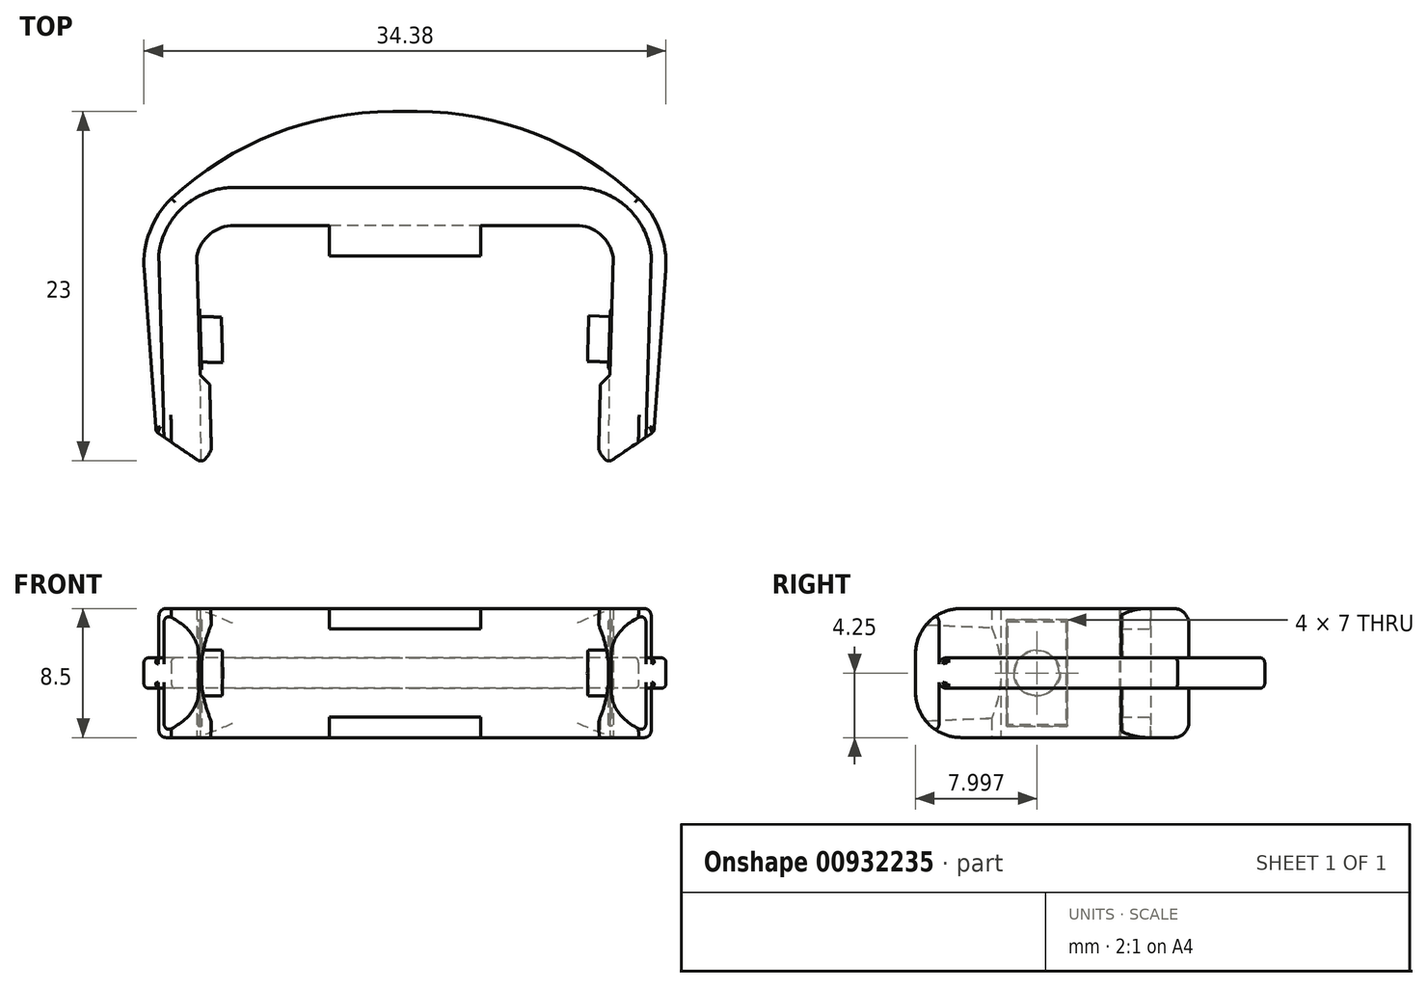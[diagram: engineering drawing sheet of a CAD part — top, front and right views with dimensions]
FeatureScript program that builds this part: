
annotation { "Feature Type Name" : "Feature", "Feature Type Description" : "" }
export const myFeature = defineFeature(function(context is Context, id is Id, definition is map)
    precondition{}
    {
        {
            var Q0;
            Q0=qCreatedBy(makeId("Top.planeOp"),FACE);
            var sketch = newSketch(context, id + "F0", { "sketchPlane" : qUnion([Q0])});
            skLineSegment(sketch, "E0", {"start": v(13.34, 0) * mm, "end": v(13.72, 13.41) * mm});
            skLineSegment(sketch, "E1", {"start": v(-13.34, 0) * mm, "end": v(-13.7, 13.5) * mm});
            skLineSegment(sketch, "E2", {"start": v(-11.25, 15.5) * mm, "end": v(11.25, 15.5) * mm});
            skArc(sketch, "E3", {"start": v(11.25, 15.5) * mm, "mid": v(12.87, 14.9) * mm, "end": v(13.72, 13.41) * mm});
            skArc(sketch, "E4", {"start": v(-11.25, 15.5) * mm, "mid": v(-12.83, 14.93) * mm, "end": v(-13.7, 13.5) * mm});
            skLineSegment(sketch, "E5", {"start": v(15.84, 0) * mm, "end": v(16.22, 13.55) * mm});
            skLineSegment(sketch, "E6", {"start": v(-11.25, 18) * mm, "end": v(11.25, 18) * mm});
            skLineSegment(sketch, "E7", {"start": v(-15.84, 0) * mm, "end": v(-16.2, 13.66) * mm});
            skLineSegment(sketch, "E8", {"start": v(-15.84, 0) * mm, "end": v(-13.33, 0) * mm});
            skLineSegment(sketch, "E9", {"start": v(13.34, 0) * mm, "end": v(15.84, 0) * mm});
            skLineSegment(sketch, "E10", {"start": v(-13.6, 0) * mm, "end": v(-18, 3) * mm});
            skLineSegment(sketch, "E11", {"start": v(13.6, 0) * mm, "end": v(18, 3) * mm});
            skLineSegment(sketch, "E12", {"start": v(-12.73, 0) * mm, "end": v(-12.87, 5) * mm});
            skLineSegment(sketch, "E13", {"start": v(12.74, 0) * mm, "end": v(12.88, 5) * mm});
            skLineSegment(sketch, "E14", {"start": v(-12.87, 5) * mm, "end": v(-13.49, 5.63) * mm});
            skLineSegment(sketch, "E15", {"start": v(12.88, 5) * mm, "end": v(13.5, 5.63) * mm});
            skLineSegment(sketch, "E16", {"start": v(-12.73, 0) * mm, "end": v(-13.33, 0) * mm});
            skLineSegment(sketch, "E17", {"start": v(12.74, 0) * mm, "end": v(13.34, 0) * mm});
            skArc(sketch, "E18", {"start": v(-11.25, 18) * mm, "mid": v(-14.54, 16.76) * mm, "end": v(-16.2, 13.66) * mm});
            skArc(sketch, "E19", {"start": v(11.25, 18) * mm, "mid": v(14.59, 16.72) * mm, "end": v(16.22, 13.55) * mm});
            skPoint(sketch, "E20", {"position": v(-14.59, 0) * mm});
            skSolve(sketch);
        }
        {
            var Q0;
            Q0 = qSketchRegion(id + "F0", true);
            extrude(context, id + "F1", {"entities" : qUnion([Q0]), "depth" : 8.5 * mm, "offsetDistance" : 25 * mm, "symmetric" : true});
        }
        {
            var Q0;
            Q0=makeQuery(id+"F1.opExtrude","CAP_EDGE",EDGE,{"disambiguationData":[OSD([sQuery(id+"F0.wireOp",EDGE,"E8")])],"isStart":false});
            var Q1;
            Q1=makeQuery(id+"F1.opExtrude","CAP_EDGE",EDGE,{"disambiguationData":[OSD([sQuery(id+"F0.wireOp",EDGE,"E8")])],"isStart":true});
            var Q2;
            Q2=makeQuery(id+"F1.opExtrude","CAP_EDGE",EDGE,{"disambiguationData":[OSD([sQuery(id+"F0.wireOp",EDGE,"E9")])],"isStart":false});
            var Q3;
            Q3=makeQuery(id+"F1.opExtrude","CAP_EDGE",EDGE,{"disambiguationData":[OSD([sQuery(id+"F0.wireOp",EDGE,"E9")])],"isStart":true});
            fillet(context, id + "F2", {"entities" : qUnion([Q0, Q1, Q2, Q3]), "radius" : 3 * mm, "tangentPropagation" : true, "allowEdgeOverflow" : false});
        }
        {
            var Q0;
            Q0=makeQuery(id+"F1.opExtrude","CAP_EDGE",EDGE,{"disambiguationData":[OSD([sQuery(id+"F0.wireOp",EDGE,"E6")])],"isStart":false});
            var Q1;
            Q1=makeQuery(id+"F1.opExtrude","CAP_EDGE",EDGE,{"disambiguationData":[OSD([sQuery(id+"F0.wireOp",EDGE,"E6")])],"isStart":true});
            fillet(context, id + "F3", {"entities" : qUnion([Q0, Q1]), "radius" : 1 * mm, "allowEdgeOverflow" : false});
        }
        {
            var Q0;
            Q0=makeQuery(id+"F1.opExtrude","CAP_EDGE",EDGE,{"disambiguationData":[OSD([sQuery(id+"F0.wireOp",EDGE,"E7")])],"isStart":true});
            var Q1;
            Q1=makeQuery(id+"F1.opExtrude","CAP_EDGE",EDGE,{"disambiguationData":[OSD([sQuery(id+"F0.wireOp",EDGE,"e52e7ded-89c3-43d7-ae40-fe6d7447af5a")])],"isStart":true});
            var Q2;
            Q2=makeQuery(id+"F1.opExtrude","CAP_EDGE",EDGE,{"disambiguationData":[OSD([sQuery(id+"F0.wireOp",EDGE,"E5")])],"isStart":true});
            var Q3;
            Q3=makeQuery(id+"F1.opExtrude","CAP_EDGE",EDGE,{"disambiguationData":[OSD([sQuery(id+"F0.wireOp",EDGE,"fc301240-3a13-4fbf-9681-00e86052290d")])],"isStart":true});
            var Q4;
            Q4=makeQuery(id+"F1.opExtrude","CAP_EDGE",EDGE,{"disambiguationData":[OSD([sQuery(id+"F0.wireOp",EDGE,"e52e7ded-89c3-43d7-ae40-fe6d7447af5a")])],"isStart":false});
            var Q5;
            Q5=makeQuery(id+"F1.opExtrude","CAP_EDGE",EDGE,{"disambiguationData":[OSD([sQuery(id+"F0.wireOp",EDGE,"E7")])],"isStart":false});
            var Q6;
            Q6=makeQuery(id+"F1.opExtrude","CAP_EDGE",EDGE,{"disambiguationData":[OSD([sQuery(id+"F0.wireOp",EDGE,"fc301240-3a13-4fbf-9681-00e86052290d")])],"isStart":false});
            var Q7;
            Q7=makeQuery(id+"F1.opExtrude","CAP_EDGE",EDGE,{"disambiguationData":[OSD([sQuery(id+"F0.wireOp",EDGE,"E5")])],"isStart":false});
            fillet(context, id + "F4", {"entities" : qUnion([Q0, Q1, Q2, Q3, Q4, Q5, Q6, Q7]), "radius" : .5 * mm, "tangentPropagation" : true, "allowEdgeOverflow" : false});
        }
        {
            var Q0;
            {var subQ0=sQuery(id+"F0.wireOp",EDGE,"E8");var subQ1=sQuery(id+"F0.wireOp",EDGE,"E7");var subQ2=makeQuery(id+"F0.imprint","INTERSECT",VERTEX,{"derivedFrom":[subQ1,subQ0]});Q0=makeQuery(id+"F0.imprint","IMPRINT",FACE,{"disambiguationData":[TD([[makeQuery(id+"F0.imprint","IMPRINT",EDGE,{"disambiguationData":[TD([[subQ2,-1.0]])],"derivedFrom":subQ1}),-1.0]])]});}
            var Q1;
            {var subQ0=sQuery(id+"F0.wireOp",EDGE,"E9");var subQ1=sQuery(id+"F0.wireOp",EDGE,"E5");var subQ2=makeQuery(id+"F0.imprint","INTERSECT",VERTEX,{"derivedFrom":[subQ1,subQ0]});Q1=makeQuery(id+"F0.imprint","IMPRINT",FACE,{"disambiguationData":[TD([[makeQuery(id+"F0.imprint","IMPRINT",EDGE,{"disambiguationData":[TD([[subQ2,-1.0]])],"derivedFrom":subQ1}),1.0]])]});}
            extrude(context, id + "F5", {"entities" : qUnion([Q0, Q1]), "operationType" : NewBodyOperationType.REMOVE, "oppositeDirection" : true, "depth" : 25 * mm, "offsetDistance" : 25 * mm, "symmetric" : true});
        }
        {
            var Q0;
            Q0=qCreatedBy(makeId("Front.planeOp"),FACE);
            var sketch = newSketch(context, id + "F6", { "sketchPlane" : qUnion([Q0])});
            skCircle(sketch, "E21", {"center": v(-5.68, 0) * mm, "radius": 7.75 * mm});
            skCircle(sketch, "E22", {"center": v(5.68, 0) * mm, "radius": 7.75 * mm});
            skSolve(sketch);
        }
        {
            var Q0;
            Q0 = qSketchRegion(id + "F6", true);
            extrude(context, id + "F7", {"entities" : qUnion([Q0]), "operationType" : NewBodyOperationType.REMOVE, "oppositeDirection" : true, "depth" : 5.7 * mm, "offsetDistance" : 25 * mm, "hasDraft" : true, "draftAngle" : .5 * degree});
        }
        {
            var Q0;
            Q0=makeQuery(id+"F1.opExtrude","SWEPT_FACE",FACE,{"disambiguationData":[OSD([sQuery(id+"F0.wireOp",EDGE,"E1")])]});
            var sketch = newSketch(context, id + "F8", { "sketchPlane" : qUnion([Q0])});
            skLineSegment(sketch, "E23.bottom", {"start": v(6.36, 3.5) * mm, "end": v(10.36, 3.5) * mm});
            skLineSegment(sketch, "E23.top", {"start": v(6.36, -3.5) * mm, "end": v(10.36, -3.5) * mm});
            skLineSegment(sketch, "E23.left", {"start": v(6.36, 3.5) * mm, "end": v(6.36, -3.5) * mm});
            skLineSegment(sketch, "E23.right", {"start": v(10.36, 3.5) * mm, "end": v(10.36, -3.5) * mm});
            skPoint(sketch, "E23.middle", {"position": v(8.36, 0) * mm});
            skPoint(sketch, "E23.middle.positionSnap0", {"position": v(6, 0) * mm});
            skPoint(sketch, "E23.centerSnap0", {"position": v(6, 0) * mm});
            skCircle(sketch, "E24", {"center": v(8.36, 0) * mm, "radius": 1.5 * mm});
            skSolve(sketch);
        }
        {
            var Q0;
            Q0=makeQuery(id+"F1.opExtrude","SWEPT_FACE",FACE,{"disambiguationData":[OSD([sQuery(id+"F0.wireOp",EDGE,"E0")])]});
            var sketch = newSketch(context, id + "F9", { "sketchPlane" : qUnion([Q0])});
            skLineSegment(sketch, "E25.bottom", {"start": v(-6.38, -3.5) * mm, "end": v(-10.38, -3.5) * mm});
            skLineSegment(sketch, "E25.top", {"start": v(-6.38, 3.5) * mm, "end": v(-10.38, 3.5) * mm});
            skLineSegment(sketch, "E25.left", {"start": v(-6.38, -3.5) * mm, "end": v(-6.38, 3.5) * mm});
            skLineSegment(sketch, "E25.right", {"start": v(-10.38, -3.5) * mm, "end": v(-10.38, 3.5) * mm});
            skPoint(sketch, "E25.middle", {"position": v(-8.38, 0) * mm});
            skCircle(sketch, "E26", {"center": v(-8.38, 0) * mm, "radius": 1.5 * mm});
            skSolve(sketch);
        }
        {
            var Q0;
            Q0=makeQuery(id+"F9.imprint","IMPRINT",FACE,{"disambiguationData":[TD([[makeQuery(id+"F9.imprint","IMPRINT",EDGE,{"derivedFrom":sQuery(id+"F9.wireOp",EDGE,"E26")}),1.0]])]});
            var Q1;
            Q1=makeQuery(id+"F8.imprint","IMPRINT",FACE,{"disambiguationData":[TD([[makeQuery(id+"F8.imprint","IMPRINT",EDGE,{"derivedFrom":sQuery(id+"F8.wireOp",EDGE,"E24")}),1.0]])]});
            extrude(context, id + "F10", {"entities" : qUnion([Q0, Q1]), "operationType" : NewBodyOperationType.ADD, "depth" : 3 * mm, "offsetDistance" : 25 * mm, "symmetric" : true});
        }
        {
            var Q0;
            Q0=makeQuery(id+"F9.imprint","IMPRINT",FACE,{"disambiguationData":[TD([[makeQuery(id+"F9.imprint","IMPRINT",EDGE,{"derivedFrom":sQuery(id+"F9.wireOp",EDGE,"E25.bottom")}),-1.0]])]});
            var Q1;
            Q1=makeQuery(id+"F9.imprint","IMPRINT",FACE,{"disambiguationData":[TD([[makeQuery(id+"F9.imprint","IMPRINT",EDGE,{"derivedFrom":sQuery(id+"F9.wireOp",EDGE,"E26")}),1.0]])]});
            var Q2;
            Q2=makeQuery(id+"F8.imprint","IMPRINT",FACE,{"disambiguationData":[TD([[makeQuery(id+"F8.imprint","IMPRINT",EDGE,{"derivedFrom":sQuery(id+"F8.wireOp",EDGE,"E23.bottom")}),-1.0]])]});
            var Q3;
            Q3=makeQuery(id+"F8.imprint","IMPRINT",FACE,{"disambiguationData":[TD([[makeQuery(id+"F8.imprint","IMPRINT",EDGE,{"derivedFrom":sQuery(id+"F8.wireOp",EDGE,"E24")}),1.0]])]});
            extrude(context, id + "F11", {"entities" : qUnion([Q0, Q1, Q2, Q3]), "operationType" : NewBodyOperationType.ADD, "depth" : .2 * mm, "offsetDistance" : 25 * mm, "symmetric" : true});
        }
        {
            var Q0;
            Q0=makeQuery(id+"F11.opExtrude","CAP_EDGE",EDGE,{"disambiguationData":[OSD([sQuery(id+"F9.wireOp",EDGE,"E25.right")])],"isStart":false});
            var Q1;
            Q1=makeQuery(id+"F11.opExtrude","CAP_EDGE",EDGE,{"disambiguationData":[OSD([sQuery(id+"F9.wireOp",EDGE,"E25.bottom")])],"isStart":false});
            var Q2;
            Q2=makeQuery(id+"F11.opExtrude","CAP_EDGE",EDGE,{"disambiguationData":[OSD([sQuery(id+"F9.wireOp",EDGE,"E25.left")])],"isStart":false});
            var Q3;
            Q3=makeQuery(id+"F11.opExtrude","CAP_EDGE",EDGE,{"disambiguationData":[OSD([sQuery(id+"F9.wireOp",EDGE,"E25.top")])],"isStart":false});
            var Q4;
            Q4=makeQuery(id+"F11.opExtrude","CAP_EDGE",EDGE,{"disambiguationData":[OSD([sQuery(id+"F8.wireOp",EDGE,"E23.right")]),OD(1.0)],"isStart":false});
            var Q5;
            Q5=makeQuery(id+"F11.opExtrude","CAP_EDGE",EDGE,{"disambiguationData":[OSD([sQuery(id+"F8.wireOp",EDGE,"E23.bottom")]),OD(1.0)],"isStart":false});
            var Q6;
            Q6=makeQuery(id+"F11.opExtrude","CAP_EDGE",EDGE,{"disambiguationData":[OSD([sQuery(id+"F8.wireOp",EDGE,"E23.top")]),OD(1.0)],"isStart":false});
            var Q7;
            Q7=makeQuery(id+"F11.opExtrude","CAP_EDGE",EDGE,{"disambiguationData":[OSD([sQuery(id+"F8.wireOp",EDGE,"E23.left")]),OD(1.0)],"isStart":false});
            chamfer(context, id + "F12", {"entities" : qUnion([Q0, Q1, Q2, Q3, Q4, Q5, Q6, Q7]), "width" : .1 * mm, "tangentPropagation" : true});
        }
        {
            var Q0;
            Q0=makeQuery(id+"F1.opExtrude","SWEPT_FACE",FACE,{"disambiguationData":[OSD([sQuery(id+"F0.wireOp",EDGE,"E2")])]});
            var sketch = newSketch(context, id + "F13", { "sketchPlane" : qUnion([Q0])});
            skLineSegment(sketch, "E27.bottom", {"start": v(4.98, 2.9) * mm, "end": v(-4.99, 2.9) * mm});
            skLineSegment(sketch, "E27.top", {"start": v(4.98, 4.25) * mm, "end": v(-4.99, 4.25) * mm});
            skLineSegment(sketch, "E27.left", {"start": v(4.98, 2.9) * mm, "end": v(4.98, 4.25) * mm});
            skLineSegment(sketch, "E27.right", {"start": v(-4.99, 2.9) * mm, "end": v(-4.99, 4.25) * mm});
            skPoint(sketch, "E27.middle", {"position": v(0, 3.58) * mm});
            skLineSegment(sketch, "E28.bottom", {"start": v(4.99, -4.25) * mm, "end": v(-4.99, -4.25) * mm});
            skLineSegment(sketch, "E28.top", {"start": v(4.99, -2.9) * mm, "end": v(-4.99, -2.9) * mm});
            skLineSegment(sketch, "E28.left", {"start": v(4.99, -4.25) * mm, "end": v(4.99, -2.9) * mm});
            skLineSegment(sketch, "E28.right", {"start": v(-4.99, -4.25) * mm, "end": v(-4.99, -2.9) * mm});
            skPoint(sketch, "E28.middle", {"position": v(0, -3.58) * mm});
            skSolve(sketch);
        }
        {
            var Q0;
            Q0=makeQuery(id+"F13.imprint","IMPRINT",FACE,{"disambiguationData":[TD([[makeQuery(id+"F13.imprint","IMPRINT",EDGE,{"derivedFrom":sQuery(id+"F13.wireOp",EDGE,"E27.bottom")}),-1.0]])]});
            var Q1;
            Q1=makeQuery(id+"F13.imprint","IMPRINT",FACE,{"disambiguationData":[TD([[makeQuery(id+"F13.imprint","IMPRINT",EDGE,{"derivedFrom":sQuery(id+"F13.wireOp",EDGE,"E28.bottom")}),1.0]])]});
            extrude(context, id + "F14", {"entities" : qUnion([Q0, Q1]), "operationType" : NewBodyOperationType.ADD, "depth" : 2 * mm, "offsetDistance" : 25 * mm});
        }
        {
            var Q0;
            Q0=qCreatedBy(makeId("Top.planeOp"),FACE);
            var sketch = newSketch(context, id + "F15", { "sketchPlane" : qUnion([Q0])});
            skLineSegment(sketch, "E29", {"start": v(-16.4, 1.91) * mm, "end": v(-17.18, 12.57) * mm});
            skArc(sketch, "E30", {"start": v(-17.18, 12.57) * mm, "mid": v(-14.74, 17.8) * mm, "end": v(-9, 18.5) * mm});
            skLineSegment(sketch, "E31", {"start": v(0, 23) * mm, "end": v(-0.8, 23) * mm});
            skArc(sketch, "E32", {"start": v(-0.8, 23) * mm, "mid": v(-8.63, 21.52) * mm, "end": v(-15.38, 17.27) * mm});
            skLineSegment(sketch, "E33", {"start": v(0, 23) * mm, "end": v(0.8, 23) * mm});
            skPoint(sketch, "E34", {"position": v(0.8, 1.58) * mm});
            skLineSegment(sketch, "E35", {"start": v(0, 23) * mm, "end": v(0, 18) * mm});
            skLineSegment(sketch, "E36", {"start": v(-9.84, 18) * mm, "end": v(0, 18) * mm});
            skLineSegment(sketch, "E37", {"start": v(-13.82, 16.03) * mm, "end": v(-9.84, 18) * mm});
            skLineSegment(sketch, "E38", {"start": v(-13.82, 16.03) * mm, "end": v(-14.97, 14.43) * mm});
            skLineSegment(sketch, "E39", {"start": v(-14.97, 14.43) * mm, "end": v(-14.97, 8.91) * mm});
            skLineSegment(sketch, "E40", {"start": v(-14.97, 8.91) * mm, "end": v(-15.88, 1.55) * mm});
            skLineSegment(sketch, "E41", {"start": v(-15.88, 1.55) * mm, "end": v(-16.4, 1.91) * mm});
            skLineSegment(sketch, "E42", {"start": v(17.18, 12.57) * mm, "end": v(16.4, 1.91) * mm});
            skLineSegment(sketch, "E43", {"start": v(16.4, 1.91) * mm, "end": v(15.8, 1.5) * mm});
            skArc(sketch, "E44", {"start": v(17.18, 12.57) * mm, "mid": v(14.8, 17.76) * mm, "end": v(9.14, 18.56) * mm});
            skArc(sketch, "E45", {"start": v(0.8, 23) * mm, "mid": v(8.63, 21.52) * mm, "end": v(15.38, 17.27) * mm});
            skLineSegment(sketch, "E46", {"start": v(0, 18) * mm, "end": v(9.84, 18) * mm});
            skLineSegment(sketch, "E47", {"start": v(9.84, 18) * mm, "end": v(14.53, 15.86) * mm});
            skLineSegment(sketch, "E48", {"start": v(14.53, 15.86) * mm, "end": v(15.46, 13.4) * mm});
            skLineSegment(sketch, "E49", {"start": v(15.46, 13.4) * mm, "end": v(15.46, 7.43) * mm});
            skLineSegment(sketch, "E50", {"start": v(15.46, 7.43) * mm, "end": v(15.8, 1.5) * mm});
            skSolve(sketch);
        }
        {
            var Q0;
            {var subQ4=sQuery(id+"F15.wireOp",EDGE,"E29");Q0=makeQuery(id+"F15.imprint","IMPRINT",FACE,{"disambiguationData":[TD([[makeQuery(id+"F15.imprint","IMPRINT",EDGE,{"derivedFrom":subQ4}),-1.0]])]});}
            var Q1;
            {var subQ5=sQuery(id+"F15.wireOp",EDGE,"E33");Q1=makeQuery(id+"F15.imprint","IMPRINT",FACE,{"disambiguationData":[TD([[makeQuery(id+"F15.imprint","IMPRINT",EDGE,{"derivedFrom":subQ5}),-1.0]])]});}
            extrude(context, id + "F16", {"entities" : qUnion([Q0, Q1]), "operationType" : NewBodyOperationType.ADD, "depth" : 2 * mm, "offsetDistance" : 25 * mm, "symmetric" : true});
        }
        {
            var Q0;
            Q0=makeQuery(id+"F16.opExtrude","CAP_EDGE",EDGE,{"disambiguationData":[OSD([sQuery(id+"F15.wireOp",EDGE,"E32")])],"isStart":false});
            var Q1;
            Q1=makeQuery(id+"F16.opExtrude","CAP_EDGE",EDGE,{"disambiguationData":[OSD([sQuery(id+"F15.wireOp",EDGE,"E42")])],"isStart":false});
            var Q2;
            Q2=makeQuery(id+"F16.opExtrude","CAP_EDGE",EDGE,{"disambiguationData":[OSD([sQuery(id+"F15.wireOp",EDGE,"E29")])],"isStart":false});
            var Q3;
            Q3=makeQuery(id+"F16.opExtrude","CAP_EDGE",EDGE,{"disambiguationData":[OSD([sQuery(id+"F15.wireOp",EDGE,"E29")])],"isStart":true});
            var Q4;
            Q4=makeQuery(id+"F16.opExtrude","CAP_EDGE",EDGE,{"disambiguationData":[OSD([sQuery(id+"F15.wireOp",EDGE,"E32")])],"isStart":true});
            var Q5;
            Q5=makeQuery(id+"F16.opExtrude","CAP_EDGE",EDGE,{"disambiguationData":[OSD([sQuery(id+"F15.wireOp",EDGE,"E42")])],"isStart":true});
            fillet(context, id + "F17", {"entities" : qUnion([Q0, Q1, Q2, Q3, Q4, Q5]), "radius" : .3 * mm, "tangentPropagation" : true, "allowEdgeOverflow" : false});
        }
        {
            var Q0;
            Q0=makeQuery(id+"F16.opExtrude","SWEPT_EDGE",EDGE,{"disambiguationData":[OSD([sQuery(id+"F15.wireOp",EDGE,"E29"),sQuery(id+"F15.wireOp",EDGE,"E41")])]});
            var Q1;
            Q1=makeQuery(id+"F16.opExtrude","SWEPT_EDGE",EDGE,{"disambiguationData":[OSD([sQuery(id+"F15.wireOp",EDGE,"E42"),sQuery(id+"F15.wireOp",EDGE,"E43")])]});
            fillet(context, id + "F18", {"entities" : qUnion([Q0, Q1]), "radius" : .4 * mm, "tangentPropagation" : true, "allowEdgeOverflow" : false});
        }
    });
